# Revit family: 05-26-001-DN50-300
name_source: partatom
category: Pipe Accessories
units: mm (PartAtom-declared; Revit-internal decimal feet)

## family parameters
Always vertical = Yes
Cut with Voids When Loaded = No
Part Type = Valve - Breaks Into
Round Connector Dimension = Use Diameter
Shared = No
Work Plane-Based = No

## types (13) — shared parameters
1 = 1 mm  [stored 0.00328084 ft]
3 = 3 mm  [stored 0.00984252 ft]
5 = 5 mm  [stored 0.0164042 ft]
8 = 10 mm  [stored 0.0328084 ft]
DN050_ PN10/16 = 05-066-26-0502104
DN060_ PN10/16 = 05-077-26-0602204
DN065_ PN10/16 = 05-082-26-0652104
DN080_ PN10/16 = 05-098-26-0802104
DN100_ PN10/16 = 05-118-26-1002104
DN125_ PN10/16 = 05-144-26-1252104
DN150_ PN10/16 = 05-170-26-1502104
DN200_ PN10 = 05-222-26-2002404
DN200_ PN16 = 05-222-26-2004404
DN250_ PN10 = 05-274-26-2502404
DN250_ PN16 = 05-274-26-2504404
DN300_ PN10 = 05-326-26-3002404
DN300_ PN16 = 05-326-26-3004404
Description_ = AVK COMBI-FLANGE FOR D.I. PIPES, PN 10/16
Search_table = 05-26-001-DN50-300
URL_product_pages = https://www.avkvalves.com
zero-valued in all types: Default Elevation, L4

## per-type parameters (varying)
| type | (D-Dd)1 | Bore | D | DN | Dd | Epdm | FL_T | Flange_H | L | L/2 | L1 | L2 | L9 | Thickness | Thickness1 |
| DN050_ PN10/16 | 17 mm  [stored 0.0557743 ft] | 25 mm  [stored 0.082021 ft] | 83 mm | 50 mm | 33 mm  [stored 0.108268 ft] | 5 mm  [stored 0.0164042 ft] | 10 mm  [stored 0.0328084 ft] | 7 mm  [stored 0.0229659 ft] | 48 mm  [stored 0.15748 ft] | 24 mm  [stored 0.0787402 ft] | 62 mm | 72 mm | 48 mm  [stored 0.15748 ft] | 12 mm  [stored 0.0393701 ft] | 20 mm  [stored 0.0656168 ft] |
| DN060_ PN10/16 | 17 mm  [stored 0.0557743 ft] | 30 mm  [stored 0.0984252 ft] | 88 mm | 60 mm | 39 mm | 6 mm  [stored 0.019685 ft] | 11 mm  [stored 0.0360892 ft] | 7 mm  [stored 0.0229659 ft] | 48 mm  [stored 0.15748 ft] | 24 mm  [stored 0.0787402 ft] | 74 mm | 72 mm | 57 mm | 14 mm  [stored 0.0459318 ft] | 22 mm  [stored 0.0721785 ft] |
| DN065_ PN10/16 | 18 mm  [stored 0.0590551 ft] | 33 mm  [stored 0.108268 ft] | 93 mm | 65 mm | 41 mm  [stored 0.134514 ft] | 6 mm  [stored 0.019685 ft] | 12 mm  [stored 0.0393701 ft] | 8 mm  [stored 0.0262467 ft] | 50 mm | 25 mm  [stored 0.082021 ft] | 70 mm | 75 mm | 54 mm | 14 mm  [stored 0.0459318 ft] | 23 mm  [stored 0.0754593 ft] |
| DN080_ PN10/16 | 18 mm  [stored 0.0590551 ft] | 40 mm  [stored 0.131234 ft] | 100 mm | 80 mm | 49 mm  [stored 0.160761 ft] | 5 mm  [stored 0.0164042 ft] | 12 mm  [stored 0.0393701 ft] | 8 mm  [stored 0.0262467 ft] | 54 mm | 27 mm  [stored 0.0885827 ft] | 61 mm | 81 mm | 47 mm  [stored 0.154199 ft] | 12 mm  [stored 0.0393701 ft] | 24 mm  [stored 0.0787402 ft] |
| DN100_ PN10/16 | 18 mm  [stored 0.0590551 ft] | 50 mm | 110 mm | 100 mm | 59 mm | 5 mm  [stored 0.0164042 ft] | 13 mm  [stored 0.0426509 ft] | 8 mm  [stored 0.0262467 ft] | 67 mm | 34 mm | 61 mm | 101 mm | 47 mm  [stored 0.154199 ft] | 12 mm  [stored 0.0393701 ft] | 25 mm  [stored 0.082021 ft] |
| DN125_ PN10/16 | 19 mm | 63 mm | 125 mm | 125 mm | 72 mm | 7 mm  [stored 0.0229659 ft] | 13 mm  [stored 0.0426509 ft] | 8 mm  [stored 0.0262467 ft] | 76 mm | 38 mm  [stored 0.124672 ft] | 88 mm | 114 mm | 68 mm | 18 mm  [stored 0.0590551 ft] | 26 mm |
| DN150_ PN10/16 | 20 mm  [stored 0.0656168 ft] | 75 mm | 143 mm | 150 mm | 85 mm | 7 mm  [stored 0.0229659 ft] | 14 mm  [stored 0.0459318 ft] | 9 mm  [stored 0.0295276 ft] | 73 mm | 37 mm | 87 mm | 110 mm | 67 mm | 18 mm  [stored 0.0590551 ft] | 27 mm  [stored 0.0885827 ft] |
| DN200_ PN10 | 21 mm | 100 mm | 170 mm | 200 mm | 111 mm | 7 mm  [stored 0.0229659 ft] | 16 mm  [stored 0.0524934 ft] | 9 mm  [stored 0.0295276 ft] | 87 mm | 44 mm | 81 mm | 131 mm | 62 mm | 18 mm  [stored 0.0590551 ft] | 32 mm  [stored 0.104987 ft] |
| DN200_ PN16 | 21 mm | 100 mm | 170 mm | 200 mm | 111 mm | 7 mm  [stored 0.0229659 ft] | 16 mm  [stored 0.0524934 ft] | 9 mm  [stored 0.0295276 ft] | 87 mm | 44 mm | 88 mm | 131 mm | 68 mm | 18 mm  [stored 0.0590551 ft] | 32 mm  [stored 0.104987 ft] |
| DN250_ PN10 | 21 mm | 125 mm | 198 mm | 250 mm | 137 mm | 10 mm  [stored 0.0328084 ft] | 20 mm  [stored 0.0656168 ft] | 9 mm  [stored 0.0295276 ft] | 121 mm | 61 mm | 205 mm | 182 mm | 158 mm | 25 mm  [stored 0.082021 ft] | 40 mm  [stored 0.131234 ft] |
| DN250_ PN16 | 23 mm  [stored 0.0754593 ft] | 125 mm | 203 mm | 250 mm | 137 mm | 10 mm  [stored 0.0328084 ft] | 20 mm  [stored 0.0656168 ft] | 10 mm  [stored 0.0328084 ft] | 123 mm | 62 mm | 205 mm | 185 mm | 158 mm | 25 mm  [stored 0.082021 ft] | 40 mm  [stored 0.131234 ft] |
| DN300_ PN10 | 21 mm | 150 mm | 223 mm | 300 mm | 163 mm | 14 mm  [stored 0.0459318 ft] | 23 mm  [stored 0.0754593 ft] | 9 mm  [stored 0.0295276 ft] | 127 mm | 64 mm | 211 mm | 191 mm | 162 mm | 36 mm  [stored 0.11811 ft] | 45 mm  [stored 0.147638 ft] |
| DN300_ PN16 | 23 mm  [stored 0.0754593 ft] | 150 mm | 230 mm | 300 mm | 163 mm | 14 mm  [stored 0.0459318 ft] | 23 mm  [stored 0.0754593 ft] | 10 mm  [stored 0.0328084 ft] | 127 mm | 64 mm | 211 mm | 191 mm | 162 mm | 36 mm  [stored 0.11811 ft] | 45 mm  [stored 0.147638 ft] |

note: [stored X ft] marks values corroborated as IEEE doubles in the binary element streams (Revit-internal decimal feet)

## geometry (parser evidence)
native form markers: Sweep x12
no freeform markers — native parametric forms only
